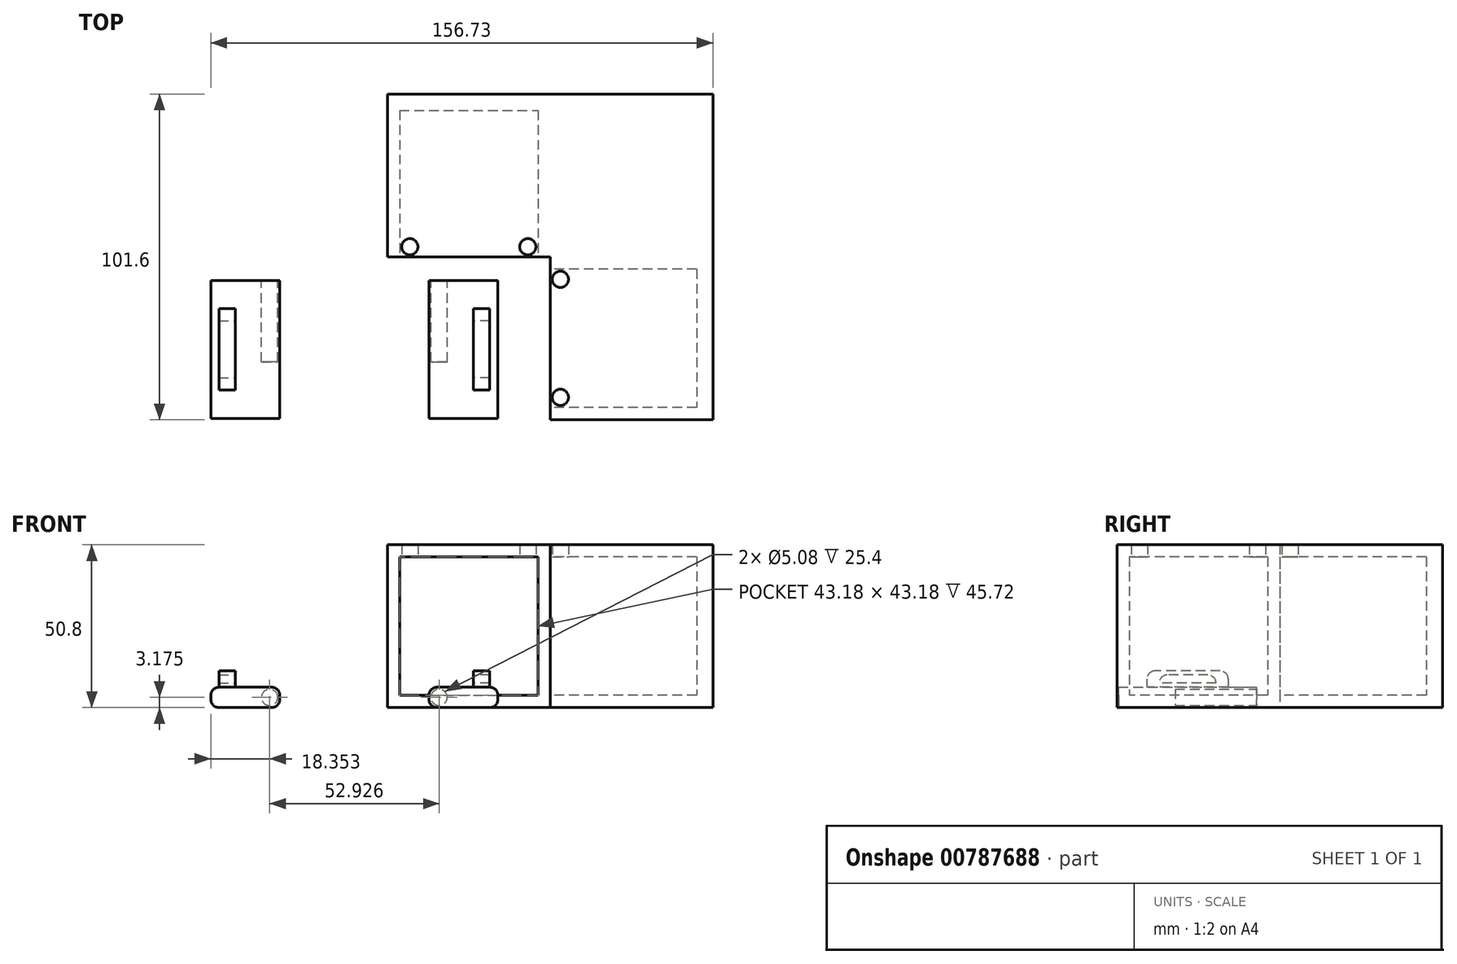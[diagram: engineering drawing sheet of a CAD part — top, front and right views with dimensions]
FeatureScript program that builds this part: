
annotation { "Feature Type Name" : "Feature", "Feature Type Description" : "" }
export const myFeature = defineFeature(function(context is Context, id is Id, definition is map)
    precondition{}
    {
        {
            var Q0;
            Q0=qCreatedBy(makeId("Top.planeOp"),FACE);
            var sketch = newSketch(context, id + "F0", { "sketchPlane" : qUnion([Q0])});
            skLineSegment(sketch, "E0.bottom", {"start": v(0, 0) * mm, "end": v(50.8, 0) * mm});
            skLineSegment(sketch, "E0.top", {"start": v(0, 50.8) * mm, "end": v(50.8, 50.8) * mm});
            skLineSegment(sketch, "E0.left", {"start": v(0, 0) * mm, "end": v(0, 50.8) * mm});
            skLineSegment(sketch, "E0.right", {"start": v(50.8, 0) * mm, "end": v(50.8, 50.8) * mm});
            skLineSegment(sketch, "E1.MirrorCS", {"start": v(0, 50.8) * mm, "end": v(-50.8, 50.8) * mm});
            skLineSegment(sketch, "E2.MirrorCS", {"start": v(-50.8, 0) * mm, "end": v(-50.8, 50.8) * mm});
            skLineSegment(sketch, "E3.MirrorCS", {"start": v(0, 0) * mm, "end": v(-50.8, 0) * mm});
            skLineSegment(sketch, "E4.MirrorCS", {"start": v(50.8, 0) * mm, "end": v(50.8, -50.8) * mm});
            skLineSegment(sketch, "E5.MirrorCS", {"start": v(0, 0) * mm, "end": v(0, -50.8) * mm});
            skLineSegment(sketch, "E6.MirrorCS", {"start": v(0, -50.8) * mm, "end": v(50.8, -50.8) * mm});
            skSolve(sketch);
        }
        {
            var Q0;
            Q0=makeQuery(id+"F0.imprint","IMPRINT",FACE,{"disambiguationData":[TD([[makeQuery(id+"F0.imprint","IMPRINT",EDGE,{"derivedFrom":sQuery(id+"F0.wireOp",EDGE,"E0.bottom")}),1.0]])]});
            var Q1;
            Q1=makeQuery(id+"F0.imprint","IMPRINT",FACE,{"disambiguationData":[TD([[makeQuery(id+"F0.imprint","IMPRINT",EDGE,{"derivedFrom":sQuery(id+"F0.wireOp",EDGE,"E0.left")}),1.0]])]});
            var Q2;
            Q2=makeQuery(id+"F0.imprint","IMPRINT",FACE,{"disambiguationData":[TD([[makeQuery(id+"F0.imprint","IMPRINT",EDGE,{"derivedFrom":sQuery(id+"F0.wireOp",EDGE,"E0.bottom")}),-1.0]])]});
            extrude(context, id + "F1", {"entities" : qUnion([Q0, Q1, Q2]), "depth" : 50.8 * mm, "offsetDistance" : 25.4 * mm});
        }
        {
            var Q0;
            Q0=makeQuery(id+"F1.opExtrude","SWEPT_FACE",FACE,{"disambiguationData":[OSD([sQuery(id+"F0.wireOp",EDGE,"E5.MirrorCS")])]});
            var sketch = newSketch(context, id + "F2", { "sketchPlane" : qUnion([Q0])});
            skPoint(sketch, "E7.middle", {"position": v(25.4, 25.4) * mm});
            skLineSegment(sketch, "E8.bottom", {"start": v(0, 50.8) * mm, "end": v(50.8, 50.8) * mm});
            skLineSegment(sketch, "E8.top", {"start": v(0, 0) * mm, "end": v(50.8, 0) * mm});
            skLineSegment(sketch, "E8.left", {"start": v(0, 50.8) * mm, "end": v(0, 0) * mm});
            skLineSegment(sketch, "E8.right", {"start": v(50.8, 50.8) * mm, "end": v(50.8, 0) * mm});
            skLineSegment(sketch, "E9.bottom", {"start": v(3.8, 47) * mm, "end": v(46.99, 47) * mm});
            skLineSegment(sketch, "E9.top", {"start": v(3.8, 3.8) * mm, "end": v(46.99, 3.8) * mm});
            skLineSegment(sketch, "E9.left", {"start": v(3.8, 47) * mm, "end": v(3.8, 3.8) * mm});
            skLineSegment(sketch, "E9.right", {"start": v(46.99, 47) * mm, "end": v(46.99, 3.8) * mm});
            skSolve(sketch);
        }
        {
            var Q0;
            Q0=makeQuery(id+"F1.opExtrude","SWEPT_FACE",FACE,{"disambiguationData":[OSD([sQuery(id+"F0.wireOp",EDGE,"E3.MirrorCS")])]});
            var sketch = newSketch(context, id + "F3", { "sketchPlane" : qUnion([Q0])});
            skLineSegment(sketch, "E10", {"start": v(-50.8, 50.8) * mm, "end": v(0, 0) * mm});
            skLineSegment(sketch, "E11.bottom", {"start": v(-46.99, 47) * mm, "end": v(-3.81, 47) * mm});
            skLineSegment(sketch, "E11.top", {"start": v(-46.99, 3.81) * mm, "end": v(-3.81, 3.81) * mm});
            skLineSegment(sketch, "E11.left", {"start": v(-46.99, 47) * mm, "end": v(-46.99, 3.81) * mm});
            skLineSegment(sketch, "E11.right", {"start": v(-3.81, 47) * mm, "end": v(-3.81, 3.81) * mm});
            skPoint(sketch, "E11.middle", {"position": v(-25.4, 25.4) * mm});
            skSolve(sketch);
        }
        {
            var Q0;
            Q0 = qSketchRegion(id + "F3", true);
            extrude(context, id + "F4", {"entities" : qUnion([Q0]), "operationType" : NewBodyOperationType.REMOVE, "oppositeDirection" : true, "depth" : 45.72 * mm, "offsetDistance" : 25.4 * mm});
        }
        {
            var Q0;
            Q0=makeQuery(id+"F4.boolean.opBoolean","COPY",FACE,{"derivedFrom":makeQuery(id+"F4.opExtrude","SWEPT_FACE",FACE,{"disambiguationData":[OSD([sQuery(id+"F3.wireOp",EDGE,"E11.bottom")])]})});
            var sketch = newSketch(context, id + "F5", { "sketchPlane" : qUnion([Q0])});
            skLineSegment(sketch, "E12", {"start": v(-46.99, 0) * mm, "end": v(-43.81, 0) * mm});
            skLineSegment(sketch, "E13", {"start": v(-43.81, 0) * mm, "end": v(-43.81, -3.18) * mm});
            skLineSegment(sketch, "E14", {"start": v(-3.81, 0) * mm, "end": v(-6.99, 0) * mm});
            skLineSegment(sketch, "E15", {"start": v(-6.99, 0) * mm, "end": v(-6.99, -3.18) * mm});
            skLineSegment(sketch, "E16", {"start": v(-6.99, -3.18) * mm, "end": v(-7.25, -3.18) * mm});
            skCircle(sketch, "E17", {"center": v(-43.81, -3.18) * mm, "radius": 2.54 * mm});
            skCircle(sketch, "E18", {"center": v(-6.99, -3.18) * mm, "radius": 2.54 * mm});
            skSolve(sketch);
        }
        {
            var Q0;
            Q0=makeQuery(id+"F5.imprint","IMPRINT",FACE,{"disambiguationData":[TD([[makeQuery(id+"F5.imprint","IMPRINT",EDGE,{"derivedFrom":sQuery(id+"F5.wireOp",EDGE,"E17")}),1.0]])]});
            var Q1;
            Q1=makeQuery(id+"F5.imprint","IMPRINT",FACE,{"disambiguationData":[TD([[makeQuery(id+"F5.imprint","IMPRINT",EDGE,{"derivedFrom":sQuery(id+"F5.wireOp",EDGE,"E18")}),1.0]])]});
            extrude(context, id + "F6", {"entities" : qUnion([Q0, Q1]), "operationType" : NewBodyOperationType.REMOVE, "oppositeDirection" : true, "depth" : 25.4 * mm, "offsetDistance" : 25.4 * mm});
        }
        {
            var Q0;
            Q0=makeQuery(id+"F2.imprint","IMPRINT",FACE,{"disambiguationData":[TD([[makeQuery(id+"F2.imprint","IMPRINT",EDGE,{"derivedFrom":sQuery(id+"F2.wireOp",EDGE,"E9.bottom")}),-1.0]])]});
            extrude(context, id + "F7", {"entities" : qUnion([Q0]), "operationType" : NewBodyOperationType.REMOVE, "oppositeDirection" : true, "depth" : 45.72 * mm, "offsetDistance" : 25.4 * mm});
        }
        {
            var Q0;
            Q0=makeQuery(id+"F7.boolean.opBoolean","COPY",FACE,{"derivedFrom":makeQuery(id+"F7.opExtrude","SWEPT_FACE",FACE,{"disambiguationData":[OSD([sQuery(id+"F2.wireOp",EDGE,"E9.bottom")])]})});
            var sketch = newSketch(context, id + "F8", { "sketchPlane" : qUnion([Q0])});
            skLineSegment(sketch, "E19", {"start": v(0, 25.4) * mm, "end": v(8.42, 25.4) * mm});
            skLineSegment(sketch, "E20", {"start": v(0, 3.8) * mm, "end": v(0, 6.98) * mm});
            skLineSegment(sketch, "E21", {"start": v(0, 6.98) * mm, "end": v(3.18, 6.98) * mm});
            skCircle(sketch, "E22", {"center": v(3.18, 6.98) * mm, "radius": 2.54 * mm});
            skCircle(sketch, "E23.MirrorC", {"center": v(3.17, 43.81) * mm, "radius": 2.54 * mm});
            skSolve(sketch);
        }
        {
            var Q0;
            Q0 = qSketchRegion(id + "F8", true);
            extrude(context, id + "F9", {"entities" : qUnion([Q0]), "operationType" : NewBodyOperationType.REMOVE, "oppositeDirection" : true, "depth" : 25.4 * mm, "offsetDistance" : 25.4 * mm});
        }
        {
            var Q0;
            Q0=qCreatedBy(makeId("Top.planeOp"),FACE);
            var sketch = newSketch(context, id + "F10", { "sketchPlane" : qUnion([Q0])});
            skLineSegment(sketch, "E24.bottom", {"start": v(-16.3, -50.35) * mm, "end": v(-37.83, -50.35) * mm});
            skLineSegment(sketch, "E24.top", {"start": v(-16.3, -7.3) * mm, "end": v(-37.83, -7.3) * mm});
            skLineSegment(sketch, "E24.left", {"start": v(-16.3, -50.35) * mm, "end": v(-16.3, -7.3) * mm});
            skLineSegment(sketch, "E24.right", {"start": v(-37.83, -50.35) * mm, "end": v(-37.83, -7.3) * mm});
            skSolve(sketch);
        }
        {
            var Q0;
            Q0 = qSketchRegion(id + "F10", true);
            extrude(context, id + "F11", {"entities" : qUnion([Q0]), "depth" : 6.35 * mm, "offsetDistance" : 25.4 * mm});
        }
        {
            var Q0;
            Q0=makeQuery(id+"F11.opExtrude","SWEPT_FACE",FACE,{"disambiguationData":[OSD([sQuery(id+"F10.wireOp",EDGE,"E24.top")])]});
            var sketch = newSketch(context, id + "F12", { "sketchPlane" : qUnion([Q0])});
            skLineSegment(sketch, "E25", {"start": v(37.83, 0) * mm, "end": v(34.65, 0) * mm});
            skLineSegment(sketch, "E26", {"start": v(34.65, 0) * mm, "end": v(34.65, 3.17) * mm});
            skCircle(sketch, "E27", {"center": v(34.65, 3.18) * mm, "radius": 2.54 * mm});
            skSolve(sketch);
        }
        {
            var Q0;
            Q0 = qSketchRegion(id + "F12", true);
            extrude(context, id + "F13", {"entities" : qUnion([Q0]), "operationType" : NewBodyOperationType.REMOVE, "oppositeDirection" : true, "depth" : 25.4 * mm, "offsetDistance" : 25.4 * mm});
        }
        {
            var Q0;
            Q0=makeQuery(id+"F11.opExtrude","CAP_FACE",FACE,{"disambiguationData":[OSD([sQuery(id+"F10.wireOp",EDGE,"E24.bottom"),sQuery(id+"F10.wireOp",EDGE,"E24.top"),sQuery(id+"F10.wireOp",EDGE,"E24.left"),sQuery(id+"F10.wireOp",EDGE,"E24.right")])],"isStart":false});
            var sketch = newSketch(context, id + "F14", { "sketchPlane" : qUnion([Q0])});
            skLineSegment(sketch, "E28", {"start": v(-16.3, -28.82) * mm, "end": v(-21.38, -28.82) * mm});
            skLineSegment(sketch, "E29.bottom", {"start": v(-18.84, -16.12) * mm, "end": v(-23.92, -16.12) * mm});
            skLineSegment(sketch, "E29.top", {"start": v(-18.84, -41.52) * mm, "end": v(-23.92, -41.52) * mm});
            skLineSegment(sketch, "E29.left", {"start": v(-18.84, -16.12) * mm, "end": v(-18.84, -41.52) * mm});
            skLineSegment(sketch, "E29.right", {"start": v(-23.92, -16.12) * mm, "end": v(-23.92, -41.52) * mm});
            skPoint(sketch, "E29.middle", {"position": v(-21.38, -28.82) * mm});
            skPoint(sketch, "E29.cornerSnap0", {"position": v(-18.84, -28.82) * mm});
            skSolve(sketch);
        }
        {
            var Q0;
            Q0 = qSketchRegion(id + "F14", true);
            extrude(context, id + "F15", {"entities" : qUnion([Q0]), "operationType" : NewBodyOperationType.ADD, "depth" : 5.08 * mm, "offsetDistance" : 25.4 * mm});
        }
        {
            var Q0;
            Q0=makeQuery(id+"F15.opExtrude","SWEPT_FACE",FACE,{"disambiguationData":[OSD([sQuery(id+"F14.wireOp",EDGE,"E29.right")])]});
            var sketch = newSketch(context, id + "F16", { "sketchPlane" : qUnion([Q0])});
            skLineSegment(sketch, "E30", {"start": v(16.12, 11.43) * mm, "end": v(41.52, 6.35) * mm});
            skLineSegment(sketch, "E31.bottom", {"start": v(37.71, 10.16) * mm, "end": v(19.93, 10.16) * mm});
            skLineSegment(sketch, "E31.top", {"start": v(37.71, 7.62) * mm, "end": v(19.93, 7.62) * mm});
            skLineSegment(sketch, "E31.left", {"start": v(37.71, 10.16) * mm, "end": v(37.71, 7.62) * mm});
            skLineSegment(sketch, "E31.right", {"start": v(19.93, 10.16) * mm, "end": v(19.93, 7.62) * mm});
            skPoint(sketch, "E31.middle", {"position": v(28.82, 8.9) * mm});
            skSolve(sketch);
        }
        {
            var Q0;
            Q0 = qSketchRegion(id + "F16", true);
            extrude(context, id + "F17", {"entities" : qUnion([Q0]), "operationType" : NewBodyOperationType.REMOVE, "oppositeDirection" : true, "depth" : 25.4 * mm, "offsetDistance" : 25.4 * mm});
        }
        {
            var Q0;
            Q0=makeQuery(id+"F15.opExtrude","CAP_EDGE",EDGE,{"disambiguationData":[OSD([sQuery(id+"F14.wireOp",EDGE,"E29.top")])],"isStart":true});
            var Q1;
            Q1=makeQuery(id+"F15.opExtrude","CAP_EDGE",EDGE,{"disambiguationData":[OSD([sQuery(id+"F14.wireOp",EDGE,"E29.top")])],"isStart":false});
            var Q2;
            Q2=makeQuery(id+"F15.opExtrude","CAP_EDGE",EDGE,{"disambiguationData":[OSD([sQuery(id+"F14.wireOp",EDGE,"E29.bottom")])],"isStart":false});
            var Q3;
            Q3=makeQuery(id+"F15.opExtrude","CAP_EDGE",EDGE,{"disambiguationData":[OSD([sQuery(id+"F14.wireOp",EDGE,"E29.bottom")])],"isStart":true});
            var Q4;
            Q4=makeQuery(id+"F17.boolean.opBoolean","COPY",EDGE,{"derivedFrom":makeQuery(id+"F17.opExtrude","SWEPT_EDGE",EDGE,{"disambiguationData":[OSD([sQuery(id+"F16.wireOp",EDGE,"E31.bottom"),sQuery(id+"F16.wireOp",EDGE,"E31.right")])]})});
            var Q5;
            Q5=makeQuery(id+"F17.boolean.opBoolean","COPY",EDGE,{"derivedFrom":makeQuery(id+"F17.opExtrude","SWEPT_EDGE",EDGE,{"disambiguationData":[OSD([sQuery(id+"F16.wireOp",EDGE,"E31.bottom"),sQuery(id+"F16.wireOp",EDGE,"E31.left")])]})});
            fillet(context, id + "F18", {"entities" : qUnion([Q0, Q1, Q2, Q3, Q4, Q5]), "radius" : 2.54 * mm, "tangentPropagation" : true, "allowEdgeOverflow" : false});
        }
        {
            var Q0;
            Q0=qCreatedBy(makeId("Top.planeOp"),FACE);
            var sketch = newSketch(context, id + "F19", { "sketchPlane" : qUnion([Q0])});
            skLineSegment(sketch, "E32", {"start": v(-61.11, -6.22) * mm, "end": v(-61.11, -40.66) * mm});
            skLineSegment(sketch, "E33.bottom", {"start": v(-61.11, -6.22) * mm, "end": v(-66.47, -6.22) * mm});
            skLineSegment(sketch, "E33.top", {"start": v(-61.11, -40.66) * mm, "end": v(-66.47, -40.66) * mm});
            skLineSegment(sketch, "E33.right", {"start": v(-66.47, -6.22) * mm, "end": v(-66.47, -40.66) * mm});
            skSolve(sketch);
        }
        {
            var Q0;
            Q0 = qSketchRegion(id + "F19", true);
            extrude(context, id + "F20", {"entities" : qUnion([Q0]), "depth" : 25.4 * mm, "offsetDistance" : 25.4 * mm});
        }
        {
            var Q0;
            Q0=makeQuery(id+"F11.opExtrude","SWEPT_BODY",BODY,{"disambiguationData":[OSD([sQuery(id+"F10.wireOp",EDGE,"E24.bottom"),sQuery(id+"F10.wireOp",EDGE,"E24.top"),sQuery(id+"F10.wireOp",EDGE,"E24.left"),sQuery(id+"F10.wireOp",EDGE,"E24.right")])]});
            var Q1;
            Q1=makeQuery(id+"F20.opExtrude","SWEPT_FACE",FACE,{"disambiguationData":[OSD([sQuery(id+"F19.wireOp",EDGE,"E32")])]});
            mirror(context, id + "F21", {"entities" : qUnion([Q0]), "mirrorPlane" : qUnion([Q1])});
        }
        {
            var Q0;
            Q0=makeQuery(id+"F20.opExtrude","CAP_FACE",FACE,{"disambiguationData":[OSD([sQuery(id+"F19.wireOp",EDGE,"E33.bottom"),sQuery(id+"F19.wireOp",EDGE,"E33.top"),sQuery(id+"F19.wireOp",EDGE,"E32"),sQuery(id+"F19.wireOp",EDGE,"E33.right")])],"isStart":false});
            extrude(context, id + "F22", {"entities" : qUnion([Q0]), "operationType" : NewBodyOperationType.REMOVE, "oppositeDirection" : true, "depth" : 25.4 * mm, "offsetDistance" : 25.4 * mm});
        }
        {
            var Q0;
            Q0=makeQuery(id+"F21.opPattern","COPY",EDGE,{"derivedFrom":makeQuery(id+"F11.opExtrude","CAP_EDGE",EDGE,{"disambiguationData":[OSD([sQuery(id+"F10.wireOp",EDGE,"E24.right")])],"isStart":false}),"instanceName":"1"});
            var Q1;
            Q1=makeQuery(id+"F11.opExtrude","CAP_EDGE",EDGE,{"disambiguationData":[OSD([sQuery(id+"F10.wireOp",EDGE,"E24.right")])],"isStart":true});
            var Q2;
            Q2=makeQuery(id+"F11.opExtrude","CAP_EDGE",EDGE,{"disambiguationData":[OSD([sQuery(id+"F10.wireOp",EDGE,"E24.right")])],"isStart":false});
            var Q3;
            Q3=makeQuery(id+"F21.opPattern","COPY",EDGE,{"derivedFrom":makeQuery(id+"F11.opExtrude","CAP_EDGE",EDGE,{"disambiguationData":[OSD([sQuery(id+"F10.wireOp",EDGE,"E24.right")])],"isStart":true}),"instanceName":"1"});
            fillet(context, id + "F23", {"entities" : qUnion([Q0, Q1, Q2, Q3]), "radius" : 2.54 * mm, "tangentPropagation" : true, "allowEdgeOverflow" : false});
        }
        {
            var Q0;
            Q0=makeQuery(id+"F11.opExtrude","CAP_EDGE",EDGE,{"disambiguationData":[OSD([sQuery(id+"F10.wireOp",EDGE,"E24.left")])],"isStart":true});
            var Q1;
            Q1=makeQuery(id+"F11.opExtrude","CAP_EDGE",EDGE,{"disambiguationData":[OSD([sQuery(id+"F10.wireOp",EDGE,"E24.left")])],"isStart":false});
            var Q2;
            Q2=makeQuery(id+"F21.opPattern","COPY",EDGE,{"derivedFrom":makeQuery(id+"F11.opExtrude","CAP_EDGE",EDGE,{"disambiguationData":[OSD([sQuery(id+"F10.wireOp",EDGE,"E24.left")])],"isStart":false}),"instanceName":"1"});
            var Q3;
            Q3=makeQuery(id+"F21.opPattern","COPY",EDGE,{"derivedFrom":makeQuery(id+"F11.opExtrude","CAP_EDGE",EDGE,{"disambiguationData":[OSD([sQuery(id+"F10.wireOp",EDGE,"E24.left")])],"isStart":true}),"instanceName":"1"});
            fillet(context, id + "F24", {"entities" : qUnion([Q0, Q1, Q2, Q3]), "radius" : 2.54 * mm, "tangentPropagation" : true, "allowEdgeOverflow" : false});
        }
    });
